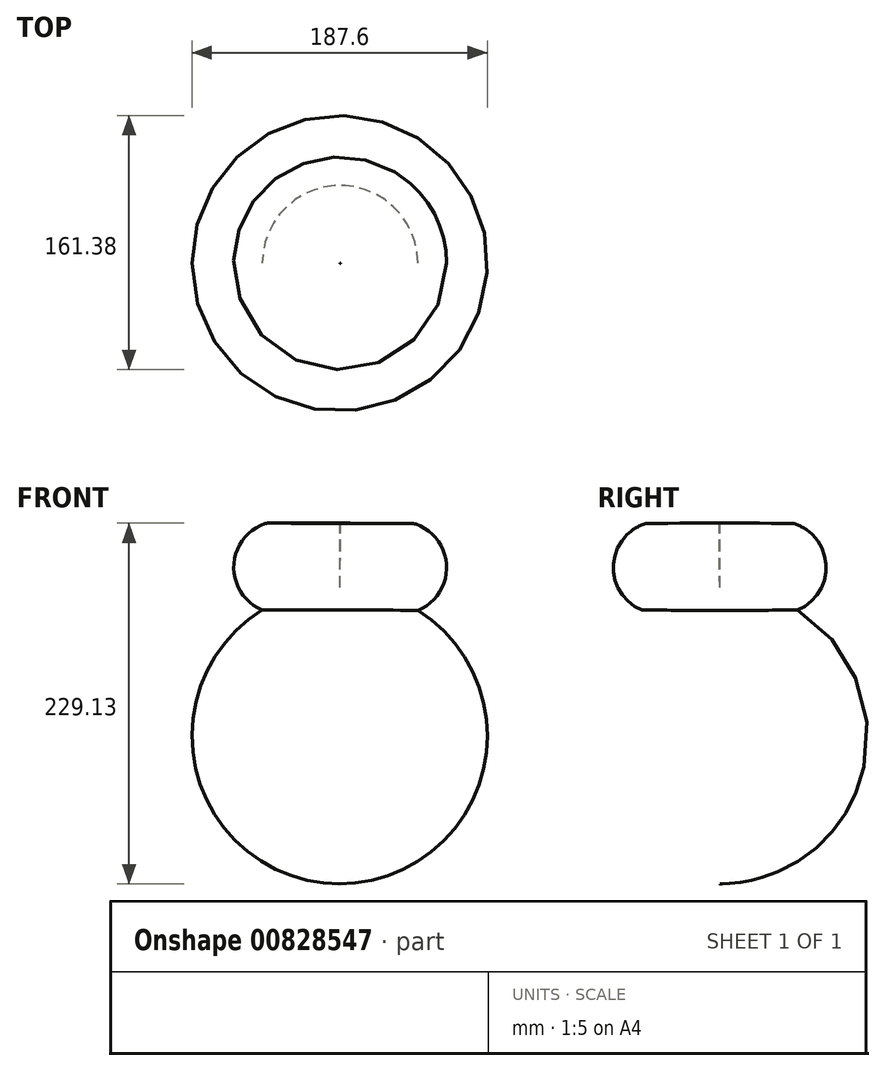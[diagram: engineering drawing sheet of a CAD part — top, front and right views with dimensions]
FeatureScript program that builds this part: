
annotation { "Feature Type Name" : "Feature", "Feature Type Description" : "" }
export const myFeature = defineFeature(function(context is Context, id is Id, definition is map)
    precondition{}
    {
        {
            var Q0;
            Q0=qCreatedBy(makeId("Front.planeOp"),FACE);
            var sketch = newSketch(context, id + "F0", { "sketchPlane" : qUnion([Q0])});
            skArc(sketch, "E0", {"start": v(0, 112.85) * mm, "mid": v(-94.07, 18.78) * mm, "end": v(0, -75.29) * mm});
            skArc(sketch, "E1", {"start": v(-47.82, 153.5) * mm, "mid": v(-67.54, 126.7) * mm, "end": v(-49.44, 98.8) * mm});
            skLineSegment(sketch, "E2", {"start": v(-45.76, 153.84) * mm, "end": v(0, 153.84) * mm});
            skLineSegment(sketch, "E3", {"start": v(0, 153.84) * mm, "end": v(0, 112.85) * mm});
            skPoint(sketch, "E4.visualSharp", {"position": v(-46.75, 153.84) * mm});
            skArc(sketch, "E4.filletArc", {"start": v(-45.76, 153.84) * mm, "mid": v(-46.8, 153.75) * mm, "end": v(-47.82, 153.5) * mm});
            skLineSegment(sketch, "E5", {"start": v(0, 112.85) * mm, "end": v(-0.55, -78.47) * mm});
            skSolve(sketch);
        }
        {
            var Q0;
            {var subQ1=sQuery(id+"F0.wireOp",EDGE,"E1");Q0=makeQuery(id+"F0.imprint","IMPRINT",FACE,{"disambiguationData":[TD([[makeQuery(id+"F0.imprint","IMPRINT",EDGE,{"derivedFrom":subQ1}),1.0]])]});}
            var Q1;
            {var subQ1=sQuery(id+"F0.wireOp",EDGE,"E0");var subQ3=makeQuery(id+"F0.imprint","INTERSECT",VERTEX,{"derivedFrom":[subQ1,sQuery(id+"F0.wireOp",EDGE,"E1")]});Q1=makeQuery(id+"F0.imprint","IMPRINT",FACE,{"disambiguationData":[TD([[makeQuery(id+"F0.imprint","IMPRINT",EDGE,{"disambiguationData":[TD([[subQ3,-1.0]])],"derivedFrom":subQ1}),1.0]])]});}
            var Q2;
            Q2=sQuery(id+"F0.wireOp",EDGE,"E5");
            revolve(context, id + "F1", {"surfaceOperationType" : NewSurfaceOperationType.NEW, "entities" : qUnion([Q0, Q1]), "axis" : qUnion([Q2]), "revolveType" : RevolveType.FULL});
        }
    });
